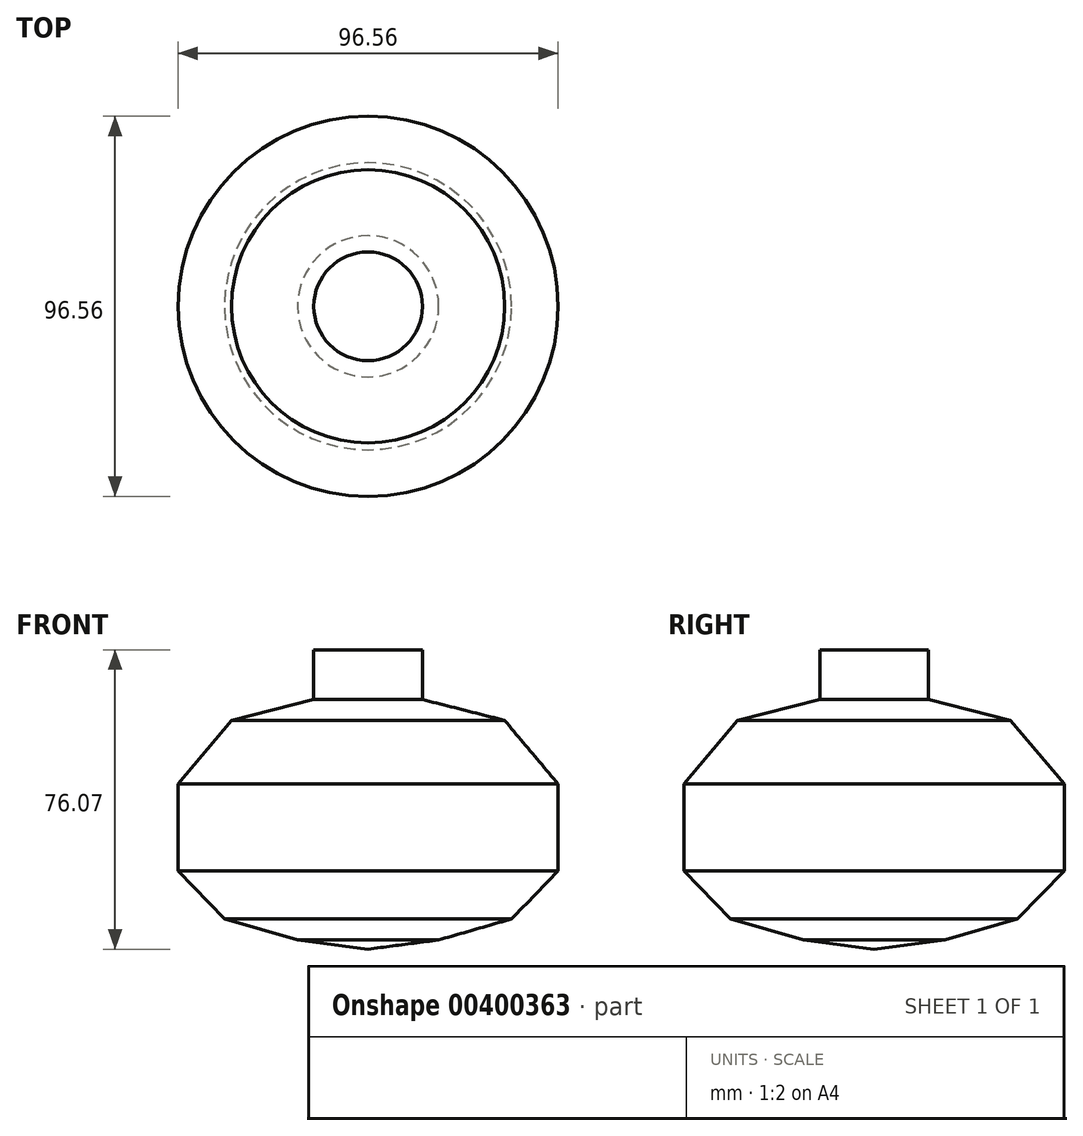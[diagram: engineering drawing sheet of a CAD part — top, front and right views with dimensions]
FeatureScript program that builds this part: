
annotation { "Feature Type Name" : "Feature", "Feature Type Description" : "" }
export const myFeature = defineFeature(function(context is Context, id is Id, definition is map)
    precondition{}
    {
        {
            var Q0;
            Q0=qCreatedBy(makeId("Front.planeOp"),FACE);
            var sketch = newSketch(context, id + "F0", { "sketchPlane" : qUnion([Q0])});
            skLineSegment(sketch, "E0", {"start": v(0, 76.07) * mm, "end": v(0, -75.67) * mm});
            skLineSegment(sketch, "E1", {"start": v(0, 76.07) * mm, "end": v(13.8, 76.07) * mm});
            skLineSegment(sketch, "E2", {"start": v(13.8, 76.07) * mm, "end": v(13.8, 63.46) * mm});
            skLineSegment(sketch, "E3", {"start": v(13.8, 63.46) * mm, "end": v(34.68, 58.14) * mm});
            skLineSegment(sketch, "E4", {"start": v(34.68, 58.14) * mm, "end": v(48.28, 41.98) * mm});
            skLineSegment(sketch, "E5", {"start": v(48.28, 41.98) * mm, "end": v(48.28, 19.9) * mm});
            skLineSegment(sketch, "E6", {"start": v(48.28, 19.9) * mm, "end": v(36.46, 7.69) * mm});
            skLineSegment(sketch, "E7", {"start": v(36.46, 7.69) * mm, "end": v(17.93, 2.36) * mm});
            skLineSegment(sketch, "E8", {"start": v(17.93, 2.36) * mm, "end": v(0, 0) * mm});
            skSolve(sketch);
        }
        {
            var Q0;
            {var subQ0=sQuery(id+"F0.wireOp",EDGE,"E1");Q0=makeQuery(id+"F0.imprint","IMPRINT",FACE,{"disambiguationData":[TD([[makeQuery(id+"F0.imprint","IMPRINT",EDGE,{"derivedFrom":subQ0}),-1.0]])]});}
            var Q1;
            Q1=sQuery(id+"F0.wireOp",EDGE,"E0");
            revolve(context, id + "F1", {"entities" : qUnion([Q0]), "axis" : qUnion([Q1]), "revolveType" : RevolveType.FULL});
        }
    });
